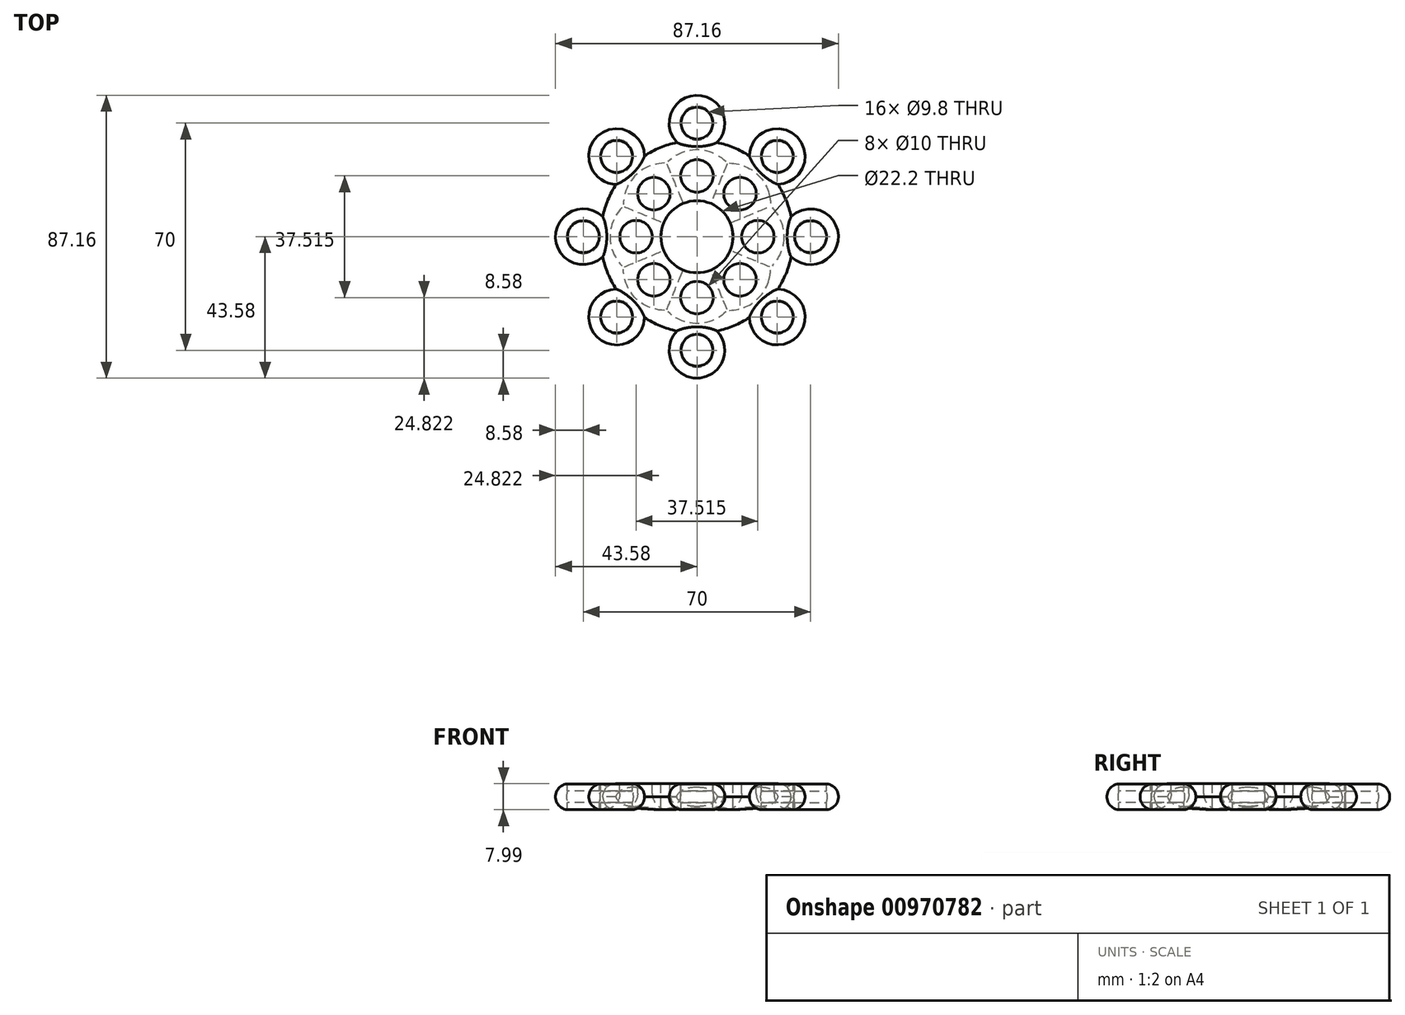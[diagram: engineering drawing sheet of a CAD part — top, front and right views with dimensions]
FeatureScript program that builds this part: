
annotation { "Feature Type Name" : "Feature", "Feature Type Description" : "" }
export const myFeature = defineFeature(function(context is Context, id is Id, definition is map)
    precondition{}
    {
        {
            var Q0;
            Q0=qCreatedBy(makeId("Front.planeOp"),FACE);
            var sketch = newSketch(context, id + "F0", { "sketchPlane" : qUnion([Q0])});
            skLineSegment(sketch, "E0.bottom", {"start": v(0, -4) * mm, "end": v(-11.1, -4) * mm});
            skLineSegment(sketch, "E0.top", {"start": v(0, 4) * mm, "end": v(-11.1, 4) * mm});
            skLineSegment(sketch, "E0.left", {"start": v(0, -4) * mm, "end": v(0, 4) * mm});
            skLineSegment(sketch, "E0.right", {"start": v(-11.1, -4) * mm, "end": v(-11.1, 4) * mm});
            skLineSegment(sketch, "E1", {"start": v(0, 37.5) * mm, "end": v(0, -37.5) * mm, "construction": true});
            skCircle(sketch, "E2", {"center": v(-35, 0) * mm, "radius": 5.2 * mm});
            skLineSegment(sketch, "E3.bottom", {"start": v(-39.9, 4) * mm, "end": v(-30.1, 4) * mm});
            skLineSegment(sketch, "E3.top", {"start": v(-39.9, -4) * mm, "end": v(-30.1, -4) * mm});
            skLineSegment(sketch, "E3.left", {"start": v(-39.9, 4) * mm, "end": v(-39.9, -4) * mm});
            skLineSegment(sketch, "E3.right", {"start": v(-30.1, 4) * mm, "end": v(-30.1, -4) * mm});
            skLineSegment(sketch, "E4", {"start": v(-35, 37.5) * mm, "end": v(-35, -37.5) * mm, "construction": true});
            skPoint(sketch, "E4.startSnap0", {"position": v(-35, 4) * mm});
            skLineSegment(sketch, "E5.bottom", {"start": v(-39.58, -4) * mm, "end": v(-26.42, -4) * mm});
            skLineSegment(sketch, "E5.top", {"start": v(-39.58, 4) * mm, "end": v(-26.42, 4) * mm});
            skLineSegment(sketch, "E5.left", {"start": v(-43.58, 0) * mm, "end": v(-43.58, 0) * mm});
            skPoint(sketch, "E6.visualSharp", {"position": v(-43.58, 4) * mm});
            skArc(sketch, "E6.filletArc", {"start": v(-39.58, 4) * mm, "mid": v(-42.41, 2.83) * mm, "end": v(-43.58, 0) * mm});
            skPoint(sketch, "E7.visualSharp", {"position": v(-43.58, -4) * mm});
            skArc(sketch, "E7.filletArc", {"start": v(-43.58, 0) * mm, "mid": v(-42.41, -2.83) * mm, "end": v(-39.58, -4) * mm});
            skLineSegment(sketch, "E8.bottom", {"start": v(-26.42, 4) * mm, "end": v(-11.1, 4) * mm});
            skLineSegment(sketch, "E8.top", {"start": v(-26.42, -4) * mm, "end": v(-11.1, -4) * mm});
            skLineSegment(sketch, "E8.right", {"start": v(-11.1, 4) * mm, "end": v(-11.1, -4) * mm});
            skPoint(sketch, "E8.middle", {"position": v(-18.76, 0) * mm});
            skLineSegment(sketch, "E9.bottom", {"start": v(-11.1, 4) * mm, "end": v(-29.8, 4) * mm});
            skLineSegment(sketch, "E9.top", {"start": v(-11.1, -3.99) * mm, "end": v(-29.8, -3.99) * mm});
            skLineSegment(sketch, "E9.left", {"start": v(-11.1, 4) * mm, "end": v(-11.1, -3.99) * mm});
            skLineSegment(sketch, "E9.right", {"start": v(-29.8, 4) * mm, "end": v(-29.8, -3.99) * mm});
            skLineSegment(sketch, "E10.bottom", {"start": v(-23.76, 4) * mm, "end": v(-18.76, 4) * mm});
            skLineSegment(sketch, "E10.top", {"start": v(-23.76, -3.99) * mm, "end": v(-18.76, -3.99) * mm});
            skLineSegment(sketch, "E10.left", {"start": v(-23.76, 4) * mm, "end": v(-23.76, -3.99) * mm});
            skLineSegment(sketch, "E10.right", {"start": v(-18.76, 4) * mm, "end": v(-18.76, -3.99) * mm});
            skSolve(sketch);
        }
        {
            var Q0;
            {var subQ1=sQuery(id+"F0.wireOp",EDGE,"E3.left");var subQ5=sQuery(id+"F0.wireOp",EDGE,"E2");var subQ6=makeQuery(id+"F0.imprint","INTERSECT",VERTEX,{"disambiguationData":[OD(0.0)],"derivedFrom":[subQ5,subQ1]});Q0=makeQuery(id+"F0.imprint","IMPRINT",FACE,{"disambiguationData":[TD([[makeQuery(id+"F0.imprint","IMPRINT",EDGE,{"disambiguationData":[TD([[subQ6,-1.0]])],"derivedFrom":subQ5}),-1.0]])]});}
            var Q1;
            Q1=sQuery(id+"F0.wireOp",EDGE,"E4");
            revolve(context, id + "F1", {"surfaceOperationType" : NewSurfaceOperationType.NEW, "entities" : qUnion([Q0]), "axis" : qUnion([Q1]), "revolveType" : RevolveType.FULL});
        }
        {
            var Q0;
            Q0=makeQuery(id+"F1.opRevolve","SWEPT_BODY",BODY,{"disambiguationData":[OSD([sQuery(id+"F0.wireOp",EDGE,"E2"),sQuery(id+"F0.wireOp",EDGE,"E3.left"),sQuery(id+"F0.wireOp",EDGE,"E6.filletArc"),sQuery(id+"F0.wireOp",EDGE,"E7.filletArc")])]});
            var Q1;
            Q1=sQuery(id+"F0.wireOp",EDGE,"E1");
            circularPattern(context, id + "F2", {"entities" : qUnion([Q0]), "axis" : qUnion([Q1]), "angle" : 360 * degree, "instanceCount" : 8, "equalSpace" : true});
        }
        {
            var Q0;
            {var subQ5=sQuery(id+"F0.wireOp",EDGE,"E10.right");Q0=makeQuery(id+"F0.imprint","IMPRINT",FACE,{"disambiguationData":[TD([[makeQuery(id+"F0.imprint","IMPRINT",EDGE,{"derivedFrom":subQ5}),1.0]])]});}
            var Q1;
            {var subQ2=sQuery(id+"F0.wireOp",EDGE,"E10.left");Q1=makeQuery(id+"F0.imprint","IMPRINT",FACE,{"disambiguationData":[TD([[makeQuery(id+"F0.imprint","IMPRINT",EDGE,{"derivedFrom":subQ2}),1.0]])]});}
            var Q2;
            {var subQ6=sQuery(id+"F0.wireOp",EDGE,"E10.left");Q2=makeQuery(id+"F0.imprint","IMPRINT",FACE,{"disambiguationData":[TD([[makeQuery(id+"F0.imprint","IMPRINT",EDGE,{"derivedFrom":subQ6}),-1.0]])]});}
            var Q3;
            Q3=sQuery(id+"F0.wireOp",EDGE,"E1");
            revolve(context, id + "F3", {"operationType" : NewBodyOperationType.ADD, "surfaceOperationType" : NewSurfaceOperationType.NEW, "entities" : qUnion([Q0, Q1, Q2]), "axis" : qUnion([Q3]), "revolveType" : RevolveType.FULL});
        }
        {
            var Q0;
            Q0=makeQuery(id+"F3.opRevolve","SWEPT_FACE",FACE,{"disambiguationData":[OSD([sQuery(id+"F0.wireOp",EDGE,"E5.top"),sQuery(id+"F0.wireOp",EDGE,"E8.bottom")])]});
            var sketch = newSketch(context, id + "F4", { "sketchPlane" : qUnion([Q0])});
            skCircle(sketch, "E11", {"center": v(-18.76, 0) * mm, "radius": 5 * mm});
            skCircle(sketch, "E12.1.0", {"center": v(-13.26, -13.26) * mm, "radius": 5 * mm});
            skCircle(sketch, "E12.2.0", {"center": v(0, -18.76) * mm, "radius": 5 * mm});
            skCircle(sketch, "E12.3.0", {"center": v(13.26, -13.26) * mm, "radius": 5 * mm});
            skCircle(sketch, "E12.4.0", {"center": v(18.76, 0) * mm, "radius": 5 * mm});
            skCircle(sketch, "E12.5.0", {"center": v(13.26, 13.26) * mm, "radius": 5 * mm});
            skCircle(sketch, "E12.6.0", {"center": v(0, 18.76) * mm, "radius": 5 * mm});
            skCircle(sketch, "E12.7.0", {"center": v(-13.26, 13.26) * mm, "radius": 5 * mm});
            skPoint(sketch, "E12.center", {"position": v(0, 0) * mm});
            skSolve(sketch);
        }
        {
            var Q0;
            Q0=makeQuery(id+"F4.imprint","IMPRINT",FACE,{"disambiguationData":[TD([[makeQuery(id+"F4.imprint","IMPRINT",EDGE,{"derivedFrom":sQuery(id+"F4.wireOp",EDGE,"E12.7.0")}),1.0]])]});
            var Q1;
            Q1=makeQuery(id+"F4.imprint","IMPRINT",FACE,{"disambiguationData":[TD([[makeQuery(id+"F4.imprint","IMPRINT",EDGE,{"derivedFrom":sQuery(id+"F4.wireOp",EDGE,"E12.6.0")}),1.0]])]});
            var Q2;
            Q2=makeQuery(id+"F4.imprint","IMPRINT",FACE,{"disambiguationData":[TD([[makeQuery(id+"F4.imprint","IMPRINT",EDGE,{"derivedFrom":sQuery(id+"F4.wireOp",EDGE,"E12.5.0")}),1.0]])]});
            var Q3;
            Q3=makeQuery(id+"F4.imprint","IMPRINT",FACE,{"disambiguationData":[TD([[makeQuery(id+"F4.imprint","IMPRINT",EDGE,{"derivedFrom":sQuery(id+"F4.wireOp",EDGE,"E12.4.0")}),1.0]])]});
            var Q4;
            Q4=makeQuery(id+"F4.imprint","IMPRINT",FACE,{"disambiguationData":[TD([[makeQuery(id+"F4.imprint","IMPRINT",EDGE,{"derivedFrom":sQuery(id+"F4.wireOp",EDGE,"E12.3.0")}),1.0]])]});
            var Q5;
            Q5=makeQuery(id+"F4.imprint","IMPRINT",FACE,{"disambiguationData":[TD([[makeQuery(id+"F4.imprint","IMPRINT",EDGE,{"derivedFrom":sQuery(id+"F4.wireOp",EDGE,"E12.2.0")}),1.0]])]});
            var Q6;
            Q6=makeQuery(id+"F4.imprint","IMPRINT",FACE,{"disambiguationData":[TD([[makeQuery(id+"F4.imprint","IMPRINT",EDGE,{"derivedFrom":sQuery(id+"F4.wireOp",EDGE,"E12.1.0")}),1.0]])]});
            var Q7;
            Q7=makeQuery(id+"F4.imprint","IMPRINT",FACE,{"disambiguationData":[TD([[makeQuery(id+"F4.imprint","IMPRINT",EDGE,{"derivedFrom":sQuery(id+"F4.wireOp",EDGE,"E11")}),1.0]])]});
            extrude(context, id + "F5", {"entities" : qUnion([Q0, Q1, Q2, Q3, Q4, Q5, Q6, Q7]), "operationType" : NewBodyOperationType.REMOVE, "oppositeDirection" : true, "depth" : 25 * mm, "offsetDistance" : 25 * mm});
        }
        {
            var Q0;
            Q0=makeQuery(id+"F3.opRevolve","SWEPT_EDGE",EDGE,{"disambiguationData":[OSD([sQuery(id+"F0.wireOp",EDGE,"E5.top"),sQuery(id+"F0.wireOp",EDGE,"E9.right")])]});
            var Q1;
            Q1=makeQuery(id+"F5.boolean.opBoolean","COPY",EDGE,{"derivedFrom":makeQuery(id+"F5.opExtrude","CAP_EDGE",EDGE,{"disambiguationData":[OSD([sQuery(id+"F4.wireOp",EDGE,"E11")])],"isStart":true})});
            var Q2;
            Q2=makeQuery(id+"F5.boolean.opBoolean","COPY",EDGE,{"derivedFrom":makeQuery(id+"F5.opExtrude","CAP_EDGE",EDGE,{"disambiguationData":[OSD([sQuery(id+"F4.wireOp",EDGE,"E12.1.0")])],"isStart":true})});
            var Q3;
            Q3=makeQuery(id+"F5.boolean.opBoolean","COPY",EDGE,{"derivedFrom":makeQuery(id+"F5.opExtrude","CAP_EDGE",EDGE,{"disambiguationData":[OSD([sQuery(id+"F4.wireOp",EDGE,"E12.2.0")])],"isStart":true})});
            var Q4;
            Q4=makeQuery(id+"F5.boolean.opBoolean","COPY",EDGE,{"derivedFrom":makeQuery(id+"F5.opExtrude","CAP_EDGE",EDGE,{"disambiguationData":[OSD([sQuery(id+"F4.wireOp",EDGE,"E12.3.0")])],"isStart":true})});
            var Q5;
            Q5=makeQuery(id+"F5.boolean.opBoolean","COPY",EDGE,{"derivedFrom":makeQuery(id+"F5.opExtrude","CAP_EDGE",EDGE,{"disambiguationData":[OSD([sQuery(id+"F4.wireOp",EDGE,"E12.4.0")])],"isStart":true})});
            var Q6;
            Q6=makeQuery(id+"F5.boolean.opBoolean","COPY",EDGE,{"derivedFrom":makeQuery(id+"F5.opExtrude","CAP_EDGE",EDGE,{"disambiguationData":[OSD([sQuery(id+"F4.wireOp",EDGE,"E12.5.0")])],"isStart":true})});
            var Q7;
            Q7=makeQuery(id+"F5.boolean.opBoolean","COPY",EDGE,{"derivedFrom":makeQuery(id+"F5.opExtrude","CAP_EDGE",EDGE,{"disambiguationData":[OSD([sQuery(id+"F4.wireOp",EDGE,"E12.6.0")])],"isStart":true})});
            var Q8;
            Q8=makeQuery(id+"F5.boolean.opBoolean","COPY",EDGE,{"derivedFrom":makeQuery(id+"F5.opExtrude","CAP_EDGE",EDGE,{"disambiguationData":[OSD([sQuery(id+"F4.wireOp",EDGE,"E12.7.0")])],"isStart":true})});
            fillet(context, id + "F6", {"entities" : qUnion([Q0, Q1, Q2, Q3, Q4, Q5, Q6, Q7, Q8]), "radius" : 5 * mm, "tangentPropagation" : true, "allowEdgeOverflow" : false});
        }
        {
            var Q0;
            Q0=makeQuery(id+"F3.opRevolve","SWEPT_EDGE",EDGE,{"disambiguationData":[OSD([sQuery(id+"F0.wireOp",EDGE,"E9.top"),sQuery(id+"F0.wireOp",EDGE,"E9.right")])]});
            var Q1;
            Q1=makeQuery(id+"F5.boolean.opBoolean","INTERSECT",EDGE,{"derivedFrom":[makeQuery(id+"F3.opRevolve","SWEPT_FACE",FACE,{"disambiguationData":[OSD([sQuery(id+"F0.wireOp",EDGE,"E9.top")])]}),makeQuery(id+"F5.opExtrude","SWEPT_FACE",FACE,{"disambiguationData":[OSD([sQuery(id+"F4.wireOp",EDGE,"E12.5.0")])]})]});
            var Q2;
            Q2=makeQuery(id+"F5.boolean.opBoolean","INTERSECT",EDGE,{"derivedFrom":[makeQuery(id+"F3.opRevolve","SWEPT_FACE",FACE,{"disambiguationData":[OSD([sQuery(id+"F0.wireOp",EDGE,"E9.top")])]}),makeQuery(id+"F5.opExtrude","SWEPT_FACE",FACE,{"disambiguationData":[OSD([sQuery(id+"F4.wireOp",EDGE,"E12.6.0")])]})]});
            var Q3;
            Q3=makeQuery(id+"F5.boolean.opBoolean","INTERSECT",EDGE,{"derivedFrom":[makeQuery(id+"F3.opRevolve","SWEPT_FACE",FACE,{"disambiguationData":[OSD([sQuery(id+"F0.wireOp",EDGE,"E9.top")])]}),makeQuery(id+"F5.opExtrude","SWEPT_FACE",FACE,{"disambiguationData":[OSD([sQuery(id+"F4.wireOp",EDGE,"E12.7.0")])]})]});
            var Q4;
            Q4=makeQuery(id+"F5.boolean.opBoolean","INTERSECT",EDGE,{"derivedFrom":[makeQuery(id+"F3.opRevolve","SWEPT_FACE",FACE,{"disambiguationData":[OSD([sQuery(id+"F0.wireOp",EDGE,"E9.top")])]}),makeQuery(id+"F5.opExtrude","SWEPT_FACE",FACE,{"disambiguationData":[OSD([sQuery(id+"F4.wireOp",EDGE,"E11")])]})]});
            var Q5;
            Q5=makeQuery(id+"F5.boolean.opBoolean","INTERSECT",EDGE,{"derivedFrom":[makeQuery(id+"F3.opRevolve","SWEPT_FACE",FACE,{"disambiguationData":[OSD([sQuery(id+"F0.wireOp",EDGE,"E9.top")])]}),makeQuery(id+"F5.opExtrude","SWEPT_FACE",FACE,{"disambiguationData":[OSD([sQuery(id+"F4.wireOp",EDGE,"E12.1.0")])]})]});
            var Q6;
            Q6=makeQuery(id+"F5.boolean.opBoolean","INTERSECT",EDGE,{"derivedFrom":[makeQuery(id+"F3.opRevolve","SWEPT_FACE",FACE,{"disambiguationData":[OSD([sQuery(id+"F0.wireOp",EDGE,"E9.top")])]}),makeQuery(id+"F5.opExtrude","SWEPT_FACE",FACE,{"disambiguationData":[OSD([sQuery(id+"F4.wireOp",EDGE,"E12.2.0")])]})]});
            var Q7;
            Q7=makeQuery(id+"F5.boolean.opBoolean","INTERSECT",EDGE,{"derivedFrom":[makeQuery(id+"F3.opRevolve","SWEPT_FACE",FACE,{"disambiguationData":[OSD([sQuery(id+"F0.wireOp",EDGE,"E9.top")])]}),makeQuery(id+"F5.opExtrude","SWEPT_FACE",FACE,{"disambiguationData":[OSD([sQuery(id+"F4.wireOp",EDGE,"E12.3.0")])]})]});
            var Q8;
            Q8=makeQuery(id+"F5.boolean.opBoolean","INTERSECT",EDGE,{"derivedFrom":[makeQuery(id+"F3.opRevolve","SWEPT_FACE",FACE,{"disambiguationData":[OSD([sQuery(id+"F0.wireOp",EDGE,"E9.top")])]}),makeQuery(id+"F5.opExtrude","SWEPT_FACE",FACE,{"disambiguationData":[OSD([sQuery(id+"F4.wireOp",EDGE,"E12.4.0")])]})]});
            fillet(context, id + "F7", {"entities" : qUnion([Q0, Q1, Q2, Q3, Q4, Q5, Q6, Q7, Q8]), "radius" : 5 * mm, "tangentPropagation" : true, "allowEdgeOverflow" : false});
        }
    });
